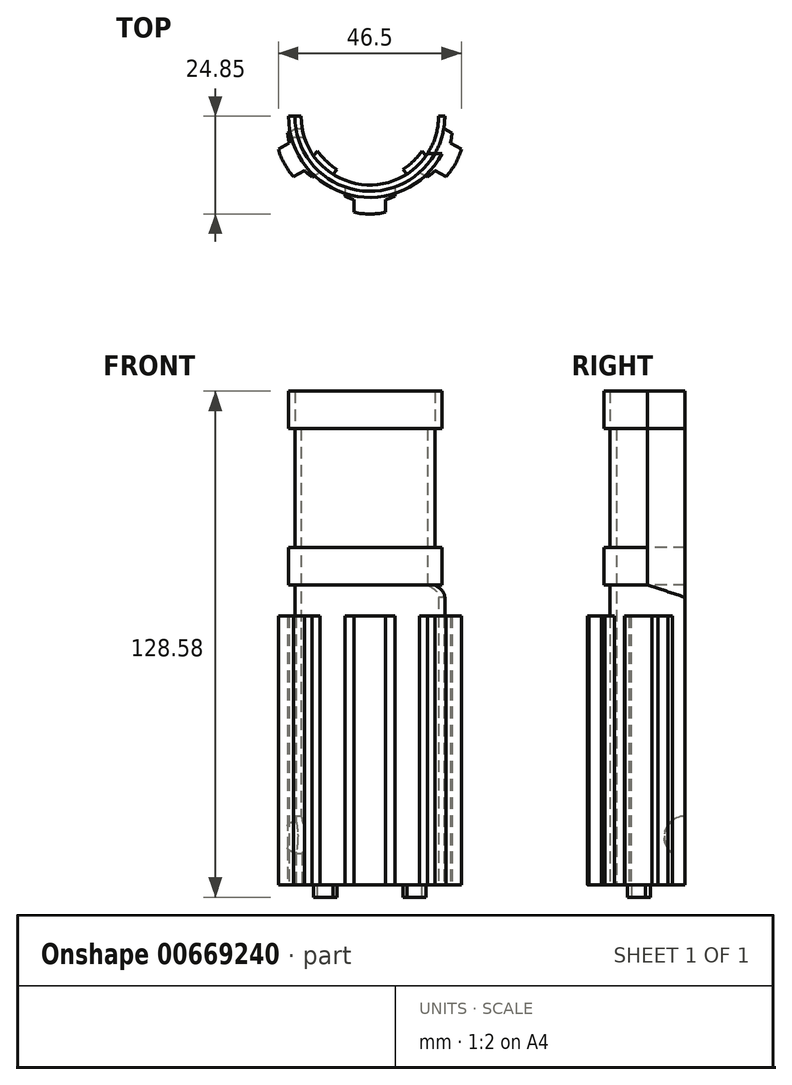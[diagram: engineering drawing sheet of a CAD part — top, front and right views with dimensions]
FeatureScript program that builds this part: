
annotation { "Feature Type Name" : "Feature", "Feature Type Description" : "" }
export const myFeature = defineFeature(function(context is Context, id is Id, definition is map)
    precondition{}
    {
        {
            var Q0;
            Q0=qCreatedBy(makeId("Top.planeOp"),FACE);
            var sketch = newSketch(context, id + "F0", { "sketchPlane" : qUnion([Q0])});
            skLineSegment(sketch, "E0", {"start": v(0, 0) * mm, "end": v(0, -19.05) * mm, "construction": true});
            skArc(sketch, "E1", {"start": v(-19.05, 0) * mm, "mid": v(0, -19.05) * mm, "end": v(19.05, 0) * mm});
            skArc(sketch, "E2.0", {"start": v(-17.46, 0) * mm, "mid": v(0, -17.46) * mm, "end": v(17.46, 0) * mm});
            skLineSegment(sketch, "E3", {"start": v(17.46, 0) * mm, "end": v(19.05, 0) * mm});
            skLineSegment(sketch, "E4", {"start": v(-17.46, 0) * mm, "end": v(-19.05, 0) * mm});
            skSolve(sketch);
        }
        {
            var Q0;
            Q0 = qSketchRegion(id + "F0", true);
            extrude(context, id + "F1", {"entities" : qUnion([Q0]), "depth" : 115.89 * mm, "offsetDistance" : 25.4 * mm});
        }
        {
            var Q0;
            Q0=makeQuery(id+"F1.opExtrude","CAP_FACE",FACE,{"disambiguationData":[OSD([sQuery(id+"F0.wireOp",EDGE,"E1"),sQuery(id+"F0.wireOp",EDGE,"E2.0"),sQuery(id+"F0.wireOp",EDGE,"E3"),sQuery(id+"F0.wireOp",EDGE,"E4")])],"isStart":true});
            var sketch = newSketch(context, id + "F2", { "sketchPlane" : qUnion([Q0])});
            skLineSegment(sketch, "E5", {"start": v(14.29, 10.04) * mm, "end": v(13.26, 8.83) * mm});
            skPoint(sketch, "E6", {"position": v(8.38, 13.5) * mm});
            skLineSegment(sketch, "E7", {"start": v(9.42, 14.7) * mm, "end": v(8.38, 13.5) * mm});
            skArc(sketch, "E8", {"start": v(14.29, 10.04) * mm, "mid": v(12.08, 12.61) * mm, "end": v(9.42, 14.7) * mm});
            skArc(sketch, "E9", {"start": v(13.26, 8.83) * mm, "mid": v(11.05, 11.4) * mm, "end": v(8.38, 13.5) * mm});
            skLineSegment(sketch, "E10", {"start": v(6.35, 17.96) * mm, "end": v(6.35, 20.34) * mm});
            skArc(sketch, "E11", {"start": v(6.35, 20.34) * mm, "mid": v(5.17, 20.82) * mm, "end": v(3.97, 21.22) * mm});
            skLineSegment(sketch, "E12", {"start": v(3.97, 21.22) * mm, "end": v(3.97, 24.4) * mm});
            skLineSegment(sketch, "E13.MirrorCS", {"start": v(-9.42, 14.7) * mm, "end": v(-8.38, 13.5) * mm});
            skArc(sketch, "E14.MirrorCS", {"start": v(-6.35, 20.34) * mm, "mid": v(-5.17, 20.82) * mm, "end": v(-3.97, 21.22) * mm});
            skLineSegment(sketch, "E15.MirrorCS", {"start": v(-14.29, 10.04) * mm, "end": v(-13.26, 8.83) * mm});
            skLineSegment(sketch, "E16.MirrorCS", {"start": v(-3.97, 21.22) * mm, "end": v(-3.97, 24.4) * mm});
            skLineSegment(sketch, "E17.MirrorCS", {"start": v(-6.35, 17.96) * mm, "end": v(-6.35, 20.34) * mm});
            skArc(sketch, "E18.MirrorCS", {"start": v(-13.26, 8.83) * mm, "mid": v(-11.05, 11.4) * mm, "end": v(-8.38, 13.5) * mm});
            skArc(sketch, "E19.MirrorCS", {"start": v(-14.29, 10.04) * mm, "mid": v(-12.08, 12.61) * mm, "end": v(-9.42, 14.7) * mm});
            skPoint(sketch, "E20.MirrorP", {"position": v(-8.38, 13.5) * mm});
            skArc(sketch, "E21", {"start": v(6.35, 17.96) * mm, "mid": v(0, 19.05) * mm, "end": v(-6.35, 17.96) * mm});
            skArc(sketch, "E22", {"start": v(3.97, 24.4) * mm, "mid": v(0, 24.85) * mm, "end": v(-3.97, 24.4) * mm});
            skLineSegment(sketch, "E23.1.0", {"start": v(12.61, 14.28) * mm, "end": v(14.7, 15.43) * mm});
            skArc(sketch, "E23.1.1", {"start": v(18.78, 3.18) * mm, "mid": v(16.65, 9.25) * mm, "end": v(12.61, 14.28) * mm});
            skArc(sketch, "E23.1.2", {"start": v(14.7, 15.43) * mm, "mid": v(15.68, 14.64) * mm, "end": v(16.62, 13.78) * mm});
            skArc(sketch, "E23.1.3", {"start": v(23.25, 8.38) * mm, "mid": v(21.72, 12.07) * mm, "end": v(19.4, 15.32) * mm});
            skArc(sketch, "E23.1.4", {"start": v(20.86, 4.33) * mm, "mid": v(20.71, 5.6) * mm, "end": v(20.47, 6.84) * mm});
            skLineSegment(sketch, "E23.1.5", {"start": v(16.62, 13.78) * mm, "end": v(19.4, 15.32) * mm});
            skLineSegment(sketch, "E23.1.6", {"start": v(20.47, 6.84) * mm, "end": v(23.25, 8.38) * mm});
            skLineSegment(sketch, "E23.1.7", {"start": v(18.78, 3.18) * mm, "end": v(20.86, 4.33) * mm});
            skLineSegment(sketch, "E23.anchor1", {"start": v(0, 0) * mm, "end": v(-1.4, 2.94) * mm, "construction": true});
            skLineSegment(sketch, "E23.anchor2", {"start": v(0, 0) * mm, "end": v(3.25, 0.02) * mm, "construction": true});
            skLineSegment(sketch, "E24.MirrorCS", {"start": v(-18.78, 3.18) * mm, "end": v(-20.86, 4.33) * mm});
            skArc(sketch, "E25.MirrorCS", {"start": v(-14.7, 15.43) * mm, "mid": v(-15.68, 14.64) * mm, "end": v(-16.62, 13.78) * mm});
            skArc(sketch, "E26.MirrorCS", {"start": v(-23.25, 8.38) * mm, "mid": v(-21.72, 12.07) * mm, "end": v(-19.4, 15.32) * mm});
            skLineSegment(sketch, "E27.MirrorCS", {"start": v(-20.47, 6.84) * mm, "end": v(-23.25, 8.38) * mm});
            skLineSegment(sketch, "E28.MirrorCS", {"start": v(-12.61, 14.28) * mm, "end": v(-14.7, 15.43) * mm});
            skLineSegment(sketch, "E29.MirrorCS", {"start": v(-16.62, 13.78) * mm, "end": v(-19.4, 15.32) * mm});
            skArc(sketch, "E30.MirrorCS", {"start": v(-20.86, 4.33) * mm, "mid": v(-20.71, 5.6) * mm, "end": v(-20.47, 6.84) * mm});
            skArc(sketch, "E31.MirrorCS", {"start": v(-18.78, 3.18) * mm, "mid": v(-16.65, 9.25) * mm, "end": v(-12.61, 14.28) * mm});
            skSolve(sketch);
        }
        {
            var Q0;
            {var subQ0=sQuery(id+"F2.wireOp",EDGE,"E13.MirrorCS");Q0=makeQuery(id+"F2.imprint","IMPRINT",FACE,{"disambiguationData":[TD([[makeQuery(id+"F2.imprint","IMPRINT",EDGE,{"derivedFrom":subQ0}),-1.0]])]});}
            var Q1;
            {var subQ0=sQuery(id+"F2.wireOp",EDGE,"E5");Q1=makeQuery(id+"F2.imprint","IMPRINT",FACE,{"disambiguationData":[TD([[makeQuery(id+"F2.imprint","IMPRINT",EDGE,{"derivedFrom":subQ0}),-1.0]])]});}
            extrude(context, id + "F3", {"entities" : qUnion([Q0, Q1]), "depth" : 3.17 * mm, "offsetDistance" : 25.4 * mm});
        }
        {
            var Q0;
            Q0=makeQuery(id+"F2.imprint","IMPRINT",FACE,{"disambiguationData":[TD([[makeQuery(id+"F2.imprint","IMPRINT",EDGE,{"derivedFrom":sQuery(id+"F2.wireOp",EDGE,"E10")}),1.0]])]});
            var Q1;
            Q1=makeQuery(id+"F2.imprint","IMPRINT",FACE,{"disambiguationData":[TD([[makeQuery(id+"F2.imprint","IMPRINT",EDGE,{"derivedFrom":sQuery(id+"F2.wireOp",EDGE,"E24.MirrorCS")}),-1.0]])]});
            var Q2;
            Q2=makeQuery(id+"F2.imprint","IMPRINT",FACE,{"disambiguationData":[TD([[makeQuery(id+"F2.imprint","IMPRINT",EDGE,{"derivedFrom":sQuery(id+"F2.wireOp",EDGE,"E23.1.0")}),-1.0]])]});
            extrude(context, id + "F4", {"entities" : qUnion([Q0, Q1, Q2]), "oppositeDirection" : true, "depth" : 68.26 * mm, "offsetDistance" : 25.4 * mm});
        }
        {
            var Q0;
            Q0=makeQuery(id+"F1.opExtrude","CAP_FACE",FACE,{"disambiguationData":[OSD([sQuery(id+"F0.wireOp",EDGE,"E1"),sQuery(id+"F0.wireOp",EDGE,"E2.0"),sQuery(id+"F0.wireOp",EDGE,"E3"),sQuery(id+"F0.wireOp",EDGE,"E4")])],"isStart":false});
            var sketch = newSketch(context, id + "F5", { "sketchPlane" : qUnion([Q0])});
            skLineSegment(sketch, "E32", {"start": v(19.05, 0) * mm, "end": v(20.64, 0) * mm});
            skLineSegment(sketch, "E33", {"start": v(-19.05, 0) * mm, "end": v(-20.64, 0) * mm});
            skArc(sketch, "E34", {"start": v(-20.64, 0) * mm, "mid": v(0, -20.64) * mm, "end": v(20.64, 0) * mm});
            skArc(sketch, "E35", {"start": v(-19.05, 0) * mm, "mid": v(0, -19.05) * mm, "end": v(19.05, 0) * mm});
            skSolve(sketch);
        }
        {
            var Q0;
            Q0=makeQuery(id+"F5.imprint","IMPRINT",FACE,{"disambiguationData":[TD([[makeQuery(id+"F5.imprint","IMPRINT",EDGE,{"derivedFrom":sQuery(id+"F5.wireOp",EDGE,"E32")}),-1.0]])]});
            extrude(context, id + "F6", {"entities" : qUnion([Q0]), "depth" : 9.52 * mm, "offsetDistance" : 25.4 * mm});
        }
        {
            var Q0;
            Q0=makeQuery(id+"F4.opExtrude","CAP_FACE",FACE,{"disambiguationData":[OSD([sQuery(id+"F2.wireOp",EDGE,"E10"),sQuery(id+"F2.wireOp",EDGE,"E11"),sQuery(id+"F2.wireOp",EDGE,"E12"),sQuery(id+"F2.wireOp",EDGE,"E14.MirrorCS"),sQuery(id+"F2.wireOp",EDGE,"E16.MirrorCS"),sQuery(id+"F2.wireOp",EDGE,"E17.MirrorCS"),sQuery(id+"F2.wireOp",EDGE,"E21"),sQuery(id+"F2.wireOp",EDGE,"E22")])],"isStart":false});
            cPlane(context, id + "F7", {"entities" : qUnion([Q0]), "cplaneType" : CPlaneType.OFFSET, "offset" : 7.94 * mm, "width" : 152.4 * mm, "height" : 152.4 * mm});
        }
        {
            var Q0;
            Q0=qCreatedBy(id+"F7.planeOp",FACE);
            var sketch = newSketch(context, id + "F8", { "sketchPlane" : qUnion([Q0])});
            skLineSegment(sketch, "E36", {"start": v(19.05, 0) * mm, "end": v(20.64, 0) * mm});
            skLineSegment(sketch, "E37", {"start": v(-19.05, 0) * mm, "end": v(-20.64, 0) * mm});
            skArc(sketch, "E38", {"start": v(-20.64, 0) * mm, "mid": v(0, -20.64) * mm, "end": v(20.64, 0) * mm});
            skArc(sketch, "E39", {"start": v(-19.05, 0) * mm, "mid": v(0, -19.05) * mm, "end": v(19.05, 0) * mm});
            skSolve(sketch);
        }
        {
            var Q0;
            Q0 = qSketchRegion(id + "F8", true);
            extrude(context, id + "F9", {"entities" : qUnion([Q0]), "operationType" : NewBodyOperationType.ADD, "depth" : 9.52 * mm, "offsetDistance" : 25.4 * mm});
        }
        {
            var Q0;
            Q0=qCreatedBy(makeId("Right.planeOp"),FACE);
            var sketch = newSketch(context, id + "F10", { "sketchPlane" : qUnion([Q0])});
            skPoint(sketch, "E40", {"position": v(-9.52, 76.2) * mm});
            skPoint(sketch, "E41", {"position": v(0, 73.03) * mm});
            skLineSegment(sketch, "E42", {"start": v(-9.53, 76.2) * mm, "end": v(0, 73.03) * mm});
            skLineSegment(sketch, "E43", {"start": v(-9.52, 76.2) * mm, "end": v(-9.52, 127.74) * mm});
            skLineSegment(sketch, "E44", {"start": v(-9.52, 127.74) * mm, "end": v(0, 127.74) * mm});
            skLineSegment(sketch, "E45", {"start": v(0, 127.74) * mm, "end": v(0, 73.03) * mm});
            skSolve(sketch);
        }
        {
            var Q0;
            Q0 = qSketchRegion(id + "F10", true);
            extrude(context, id + "F11", {"entities" : qUnion([Q0]), "operationType" : NewBodyOperationType.REMOVE, "depth" : 25.4 * mm, "offsetDistance" : 25.4 * mm});
        }
        {
            var Q0;
            Q0=qCreatedBy(makeId("Right.planeOp"),FACE);
            var sketch = newSketch(context, id + "F12", { "sketchPlane" : qUnion([Q0])});
            skPoint(sketch, "E46", {"position": v(0, 17.46) * mm});
            skPoint(sketch, "E47", {"position": v(-3.17, 7.94) * mm});
            skPoint(sketch, "E48.third.point", {"position": v(5.2, 13.17) * mm});
            skPoint(sketch, "E49", {"position": v(0, 6.88) * mm});
            skArc(sketch, "E50", {"start": v(0, 17.46) * mm, "mid": v(-5.02, 13.84) * mm, "end": v(-3.17, 7.94) * mm});
            skLineSegment(sketch, "E51", {"start": v(-3.17, 7.94) * mm, "end": v(-3.17, 0) * mm});
            skLineSegment(sketch, "E52", {"start": v(-3.17, 0) * mm, "end": v(0, 0) * mm});
            skLineSegment(sketch, "E53", {"start": v(0, 0) * mm, "end": v(0, 18.5) * mm});
            skLineSegment(sketch, "E54", {"start": v(0, 18.5) * mm, "end": v(0, 17.46) * mm});
            skLineSegment(sketch, "E55", {"start": v(-3.17, 7.94) * mm, "end": v(-3.17, -0.71) * mm});
            skLineSegment(sketch, "E56", {"start": v(-3.17, -0.71) * mm, "end": v(1.94, -0.71) * mm});
            skLineSegment(sketch, "E57", {"start": v(1.94, -0.71) * mm, "end": v(1.94, 17.46) * mm});
            skLineSegment(sketch, "E58", {"start": v(1.94, 17.46) * mm, "end": v(0, 17.46) * mm});
            skPoint(sketch, "E59", {"position": v(-3.18, 7.94) * mm});
            skSolve(sketch);
        }
        {
            var Q0;
            Q0 = qSketchRegion(id + "F12", true);
            extrude(context, id + "F13", {"entities" : qUnion([Q0]), "operationType" : NewBodyOperationType.REMOVE, "oppositeDirection" : true, "depth" : 25.4 * mm, "offsetDistance" : 25.4 * mm});
        }
    });
